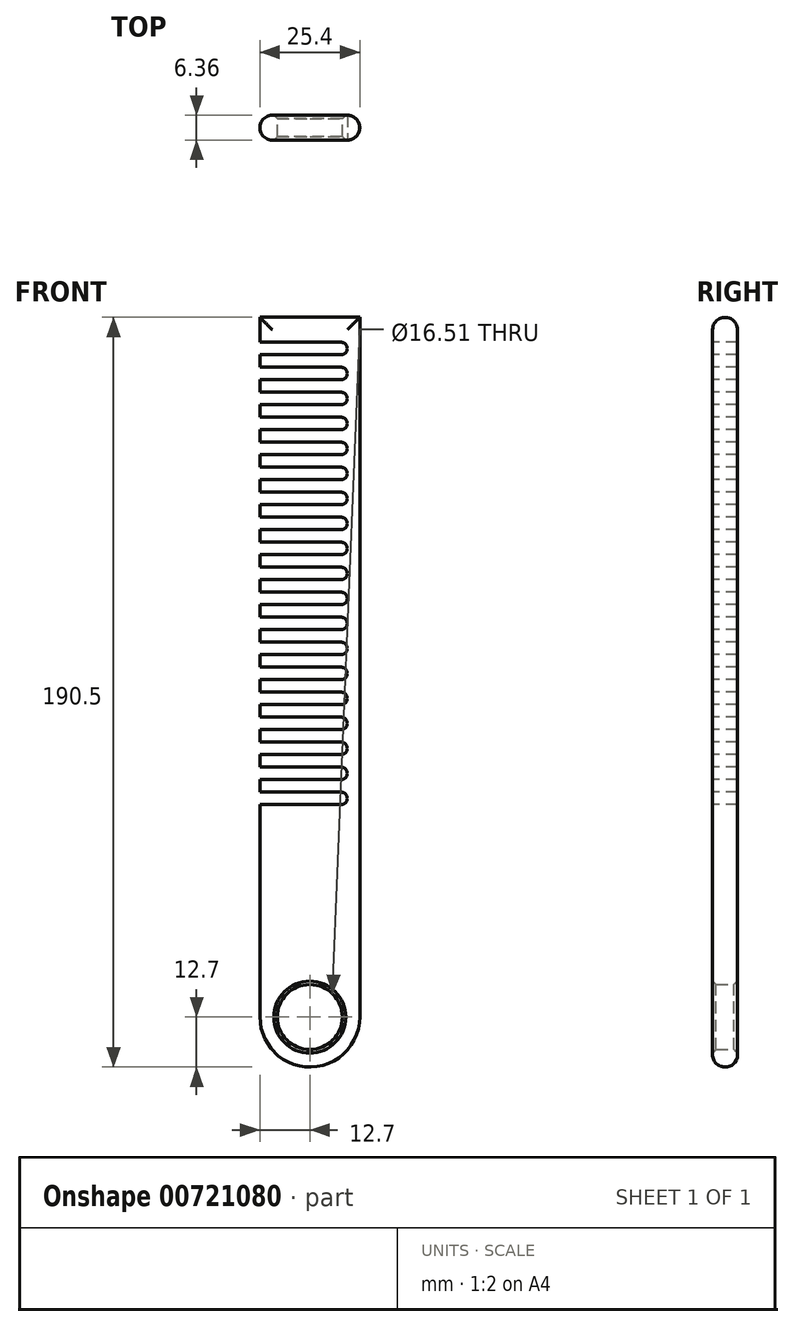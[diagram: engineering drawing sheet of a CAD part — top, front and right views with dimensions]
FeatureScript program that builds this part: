
annotation { "Feature Type Name" : "Feature", "Feature Type Description" : "" }
export const myFeature = defineFeature(function(context is Context, id is Id, definition is map)
    precondition{}
    {
        {
            var Q0;
            Q0=qCreatedBy(makeId("Front.planeOp"),FACE);
            var sketch = newSketch(context, id + "F0", { "sketchPlane" : qUnion([Q0])});
            skCircle(sketch, "E0", {"center": v(0, -63.5) * mm, "radius": 12.7 * mm});
            skCircle(sketch, "E1", {"center": v(0, -63.5) * mm, "radius": 8.26 * mm});
            skSolve(sketch);
        }
        {
            var Q0;
            Q0 = qSketchRegion(id + "F0", true);
            extrude(context, id + "F1", {"entities" : qUnion([Q0]), "endBound" : BoundingType.SYMMETRIC, "depth" : 6.35 * mm, "offsetDistance" : 25.4 * mm});
        }
        {
            var Q0;
            Q0=qCreatedBy(makeId("Front.planeOp"),FACE);
            var sketch = newSketch(context, id + "F2", { "sketchPlane" : qUnion([Q0])});
            skLineSegment(sketch, "E2.top", {"start": v(-12.7, 114.3) * mm, "end": v(12.7, 114.3) * mm});
            skLineSegment(sketch, "E2.left", {"start": v(-12.7, -63.5) * mm, "end": v(-12.7, 114.3) * mm});
            skLineSegment(sketch, "E2.right", {"start": v(12.7, -63.5) * mm, "end": v(12.7, 114.3) * mm});
            skPoint(sketch, "E2.middle", {"position": v(0, 0) * mm});
            skArc(sketch, "E3", {"start": v(12.7, -63.5) * mm, "mid": v(0, -50.8) * mm, "end": v(-12.7, -63.5) * mm});
            skPoint(sketch, "E2.bottom.end.orphan", {"position": v(12.7, -114.3) * mm});
            skPoint(sketch, "E2.bottom.start.orphan", {"position": v(-12.7, -114.3) * mm});
            skSolve(sketch);
        }
        {
            var Q0;
            Q0 = qSketchRegion(id + "F2", true);
            extrude(context, id + "F3", {"entities" : qUnion([Q0]), "operationType" : NewBodyOperationType.ADD, "endBound" : BoundingType.SYMMETRIC, "depth" : 6.35 * mm, "offsetDistance" : 25.4 * mm});
        }
        {
            var Q0;
            Q0=makeQuery(id+"F3.opExtrude","CAP_EDGE",EDGE,{"disambiguationData":[OSD([sQuery(id+"F2.wireOp",EDGE,"E2.right")])],"isStart":false});
            var Q1;
            Q1=makeQuery(id+"F3.opExtrude","CAP_EDGE",EDGE,{"disambiguationData":[OSD([sQuery(id+"F2.wireOp",EDGE,"E2.right")])],"isStart":true});
            var Q2;
            Q2=makeQuery(id+"F3.opExtrude","CAP_EDGE",EDGE,{"disambiguationData":[OSD([sQuery(id+"F2.wireOp",EDGE,"E2.top")])],"isStart":false});
            var Q3;
            Q3=makeQuery(id+"F3.opExtrude","CAP_EDGE",EDGE,{"disambiguationData":[OSD([sQuery(id+"F2.wireOp",EDGE,"E2.top")])],"isStart":true});
            fillet(context, id + "F4", {"entities" : qUnion([Q0, Q1, Q2, Q3]), "radius" : 3.17 * mm, "tangentPropagation" : true, "allowEdgeOverflow" : false});
        }
        {
            var Q0;
            Q0=makeQuery(id+"F1.opExtrude","CAP_EDGE",EDGE,{"disambiguationData":[OSD([sQuery(id+"F0.wireOp",EDGE,"E1")])],"isStart":false});
            var Q1;
            Q1=makeQuery(id+"F1.opExtrude","CAP_EDGE",EDGE,{"disambiguationData":[OSD([sQuery(id+"F0.wireOp",EDGE,"E1")])],"isStart":true});
            chamfer(context, id + "F5", {"entities" : qUnion([Q0, Q1]), "width" : 0.89 * mm, "tangentPropagation" : true});
        }
        {
            var Q0;
            Q0=makeQuery(id+"F3.boolean.opBoolean","MERGE",FACE,{"derivedFrom":[makeQuery(id+"F1.opExtrude","CAP_FACE",FACE,{"disambiguationData":[OSD([sQuery(id+"F0.wireOp",EDGE,"E0"),sQuery(id+"F0.wireOp",EDGE,"E1")])],"isStart":false}),makeQuery(id+"F3.opExtrude","CAP_FACE",FACE,{"disambiguationData":[OSD([sQuery(id+"F2.wireOp",EDGE,"E2.top"),sQuery(id+"F2.wireOp",EDGE,"E2.left"),sQuery(id+"F2.wireOp",EDGE,"E2.right"),sQuery(id+"F2.wireOp",EDGE,"E3")])],"isStart":false})]});
            var sketch = newSketch(context, id + "F6", { "sketchPlane" : qUnion([Q0])});
            skLineSegment(sketch, "E4", {"start": v(9.52, 111.12) * mm, "end": v(9.52, 107.95) * mm});
            skLineSegment(sketch, "E5", {"start": v(9.52, 111.12) * mm, "end": v(-9.53, 111.12) * mm});
            skLineSegment(sketch, "E6", {"start": v(9.52, 107.95) * mm, "end": v(-16.08, 107.95) * mm});
            skLineSegment(sketch, "E7", {"start": v(-16.08, 111.12) * mm, "end": v(-9.53, 111.12) * mm});
            skArc(sketch, "E8", {"start": v(-16.08, 111.12) * mm, "mid": v(-17.67, 109.54) * mm, "end": v(-16.08, 107.95) * mm});
            skPoint(sketch, "E9.center.orphan", {"position": v(0, -63.5) * mm});
            skLineSegment(sketch, "E10.0.1.0", {"start": v(9.52, 104.77) * mm, "end": v(9.52, 101.6) * mm});
            skLineSegment(sketch, "E10.0.1.1", {"start": v(9.52, 104.77) * mm, "end": v(-9.53, 104.77) * mm});
            skLineSegment(sketch, "E10.0.1.2", {"start": v(9.52, 101.6) * mm, "end": v(-16.08, 101.6) * mm});
            skArc(sketch, "E10.0.1.3", {"start": v(-16.08, 104.77) * mm, "mid": v(-17.67, 103.19) * mm, "end": v(-16.08, 101.6) * mm});
            skLineSegment(sketch, "E10.0.1.4", {"start": v(-16.08, 104.77) * mm, "end": v(-9.53, 104.77) * mm});
            skLineSegment(sketch, "E10.0.2.0", {"start": v(9.52, 98.42) * mm, "end": v(9.52, 95.25) * mm});
            skLineSegment(sketch, "E10.0.2.1", {"start": v(9.52, 98.42) * mm, "end": v(-9.53, 98.42) * mm});
            skLineSegment(sketch, "E10.0.2.2", {"start": v(9.52, 95.25) * mm, "end": v(-16.08, 95.25) * mm});
            skArc(sketch, "E10.0.2.3", {"start": v(-16.08, 98.42) * mm, "mid": v(-17.67, 96.84) * mm, "end": v(-16.08, 95.25) * mm});
            skLineSegment(sketch, "E10.0.2.4", {"start": v(-16.08, 98.42) * mm, "end": v(-9.53, 98.42) * mm});
            skLineSegment(sketch, "E10.direction1", {"start": v(9.52, 107.95) * mm, "end": v(-15.88, 107.95) * mm, "construction": true});
            skLineSegment(sketch, "E10.direction2", {"start": v(9.52, 107.95) * mm, "end": v(9.52, 101.6) * mm, "construction": true});
            skLineSegment(sketch, "E11.0.0.3", {"start": v(9.52, 92.07) * mm, "end": v(9.52, 88.9) * mm});
            skLineSegment(sketch, "E11.3.0.3", {"start": v(9.52, 92.07) * mm, "end": v(-9.53, 92.07) * mm});
            skLineSegment(sketch, "E11.6.0.3", {"start": v(9.52, 88.9) * mm, "end": v(-16.08, 88.9) * mm});
            skArc(sketch, "E11.9.0.3", {"start": v(-16.08, 92.07) * mm, "mid": v(-17.67, 90.49) * mm, "end": v(-16.08, 88.9) * mm});
            skLineSegment(sketch, "E11.13.0.3", {"start": v(-16.08, 92.07) * mm, "end": v(-9.53, 92.07) * mm});
            skLineSegment(sketch, "E11.0.0.4", {"start": v(9.52, 85.72) * mm, "end": v(9.52, 82.55) * mm});
            skLineSegment(sketch, "E11.3.0.4", {"start": v(9.52, 85.72) * mm, "end": v(-9.53, 85.72) * mm});
            skLineSegment(sketch, "E11.6.0.4", {"start": v(9.52, 82.55) * mm, "end": v(-16.08, 82.55) * mm});
            skArc(sketch, "E11.9.0.4", {"start": v(-16.08, 85.72) * mm, "mid": v(-17.67, 84.14) * mm, "end": v(-16.08, 82.55) * mm});
            skLineSegment(sketch, "E11.13.0.4", {"start": v(-16.08, 85.72) * mm, "end": v(-9.53, 85.72) * mm});
            skLineSegment(sketch, "E12.0.0.5", {"start": v(9.52, 79.37) * mm, "end": v(9.52, 76.2) * mm});
            skLineSegment(sketch, "E12.3.0.5", {"start": v(9.52, 79.37) * mm, "end": v(-9.53, 79.37) * mm});
            skLineSegment(sketch, "E12.6.0.5", {"start": v(9.52, 76.2) * mm, "end": v(-16.08, 76.2) * mm});
            skArc(sketch, "E12.9.0.5", {"start": v(-16.08, 79.37) * mm, "mid": v(-17.67, 77.79) * mm, "end": v(-16.08, 76.2) * mm});
            skLineSegment(sketch, "E12.13.0.5", {"start": v(-16.08, 79.37) * mm, "end": v(-9.53, 79.37) * mm});
            skLineSegment(sketch, "E12.0.0.6", {"start": v(9.52, 73.02) * mm, "end": v(9.52, 69.85) * mm});
            skLineSegment(sketch, "E12.3.0.6", {"start": v(9.52, 73.02) * mm, "end": v(-9.53, 73.02) * mm});
            skLineSegment(sketch, "E12.6.0.6", {"start": v(9.52, 69.85) * mm, "end": v(-16.08, 69.85) * mm});
            skArc(sketch, "E12.9.0.6", {"start": v(-16.08, 73.02) * mm, "mid": v(-17.67, 71.44) * mm, "end": v(-16.08, 69.85) * mm});
            skLineSegment(sketch, "E12.13.0.6", {"start": v(-16.08, 73.02) * mm, "end": v(-9.53, 73.02) * mm});
            skLineSegment(sketch, "E12.0.0.7", {"start": v(9.52, 66.67) * mm, "end": v(9.52, 63.5) * mm});
            skLineSegment(sketch, "E12.3.0.7", {"start": v(9.52, 66.67) * mm, "end": v(-9.53, 66.67) * mm});
            skLineSegment(sketch, "E12.6.0.7", {"start": v(9.52, 63.5) * mm, "end": v(-16.08, 63.5) * mm});
            skArc(sketch, "E12.9.0.7", {"start": v(-16.08, 66.67) * mm, "mid": v(-17.67, 65.09) * mm, "end": v(-16.08, 63.5) * mm});
            skLineSegment(sketch, "E12.13.0.7", {"start": v(-16.08, 66.67) * mm, "end": v(-9.53, 66.67) * mm});
            skLineSegment(sketch, "E12.0.0.8", {"start": v(9.52, 60.32) * mm, "end": v(9.52, 57.15) * mm});
            skLineSegment(sketch, "E12.3.0.8", {"start": v(9.52, 60.32) * mm, "end": v(-9.53, 60.32) * mm});
            skLineSegment(sketch, "E12.6.0.8", {"start": v(9.52, 57.15) * mm, "end": v(-16.08, 57.15) * mm});
            skArc(sketch, "E12.9.0.8", {"start": v(-16.08, 60.32) * mm, "mid": v(-17.67, 58.74) * mm, "end": v(-16.08, 57.15) * mm});
            skLineSegment(sketch, "E12.13.0.8", {"start": v(-16.08, 60.32) * mm, "end": v(-9.53, 60.32) * mm});
            skLineSegment(sketch, "E12.0.0.9", {"start": v(9.52, 53.97) * mm, "end": v(9.52, 50.8) * mm});
            skLineSegment(sketch, "E12.3.0.9", {"start": v(9.52, 53.97) * mm, "end": v(-9.53, 53.97) * mm});
            skLineSegment(sketch, "E12.6.0.9", {"start": v(9.52, 50.8) * mm, "end": v(-16.08, 50.8) * mm});
            skArc(sketch, "E12.9.0.9", {"start": v(-16.08, 53.97) * mm, "mid": v(-17.67, 52.39) * mm, "end": v(-16.08, 50.8) * mm});
            skLineSegment(sketch, "E12.13.0.9", {"start": v(-16.08, 53.97) * mm, "end": v(-9.53, 53.97) * mm});
            skLineSegment(sketch, "E13.0.0.10", {"start": v(9.52, 47.62) * mm, "end": v(9.52, 44.45) * mm});
            skLineSegment(sketch, "E13.3.0.10", {"start": v(9.52, 47.62) * mm, "end": v(-9.53, 47.62) * mm});
            skLineSegment(sketch, "E13.6.0.10", {"start": v(9.52, 44.45) * mm, "end": v(-16.08, 44.45) * mm});
            skArc(sketch, "E13.9.0.10", {"start": v(-16.08, 47.62) * mm, "mid": v(-17.67, 46.04) * mm, "end": v(-16.08, 44.45) * mm});
            skLineSegment(sketch, "E13.13.0.10", {"start": v(-16.08, 47.62) * mm, "end": v(-9.53, 47.62) * mm});
            skLineSegment(sketch, "E13.0.0.11", {"start": v(9.52, 41.27) * mm, "end": v(9.52, 38.1) * mm});
            skLineSegment(sketch, "E13.3.0.11", {"start": v(9.52, 41.27) * mm, "end": v(-9.53, 41.27) * mm});
            skLineSegment(sketch, "E13.6.0.11", {"start": v(9.52, 38.1) * mm, "end": v(-16.08, 38.1) * mm});
            skArc(sketch, "E13.9.0.11", {"start": v(-16.08, 41.27) * mm, "mid": v(-17.67, 39.69) * mm, "end": v(-16.08, 38.1) * mm});
            skLineSegment(sketch, "E13.13.0.11", {"start": v(-16.08, 41.27) * mm, "end": v(-9.53, 41.27) * mm});
            skLineSegment(sketch, "E13.0.0.12", {"start": v(9.52, 34.92) * mm, "end": v(9.52, 31.75) * mm});
            skLineSegment(sketch, "E13.3.0.12", {"start": v(9.52, 34.92) * mm, "end": v(-9.53, 34.92) * mm});
            skLineSegment(sketch, "E13.6.0.12", {"start": v(9.52, 31.75) * mm, "end": v(-16.08, 31.75) * mm});
            skArc(sketch, "E13.9.0.12", {"start": v(-16.08, 34.92) * mm, "mid": v(-17.67, 33.34) * mm, "end": v(-16.08, 31.75) * mm});
            skLineSegment(sketch, "E13.13.0.12", {"start": v(-16.08, 34.92) * mm, "end": v(-9.53, 34.92) * mm});
            skLineSegment(sketch, "E13.0.0.13", {"start": v(9.52, 28.57) * mm, "end": v(9.52, 25.4) * mm});
            skLineSegment(sketch, "E13.3.0.13", {"start": v(9.52, 28.57) * mm, "end": v(-9.53, 28.57) * mm});
            skLineSegment(sketch, "E13.6.0.13", {"start": v(9.52, 25.4) * mm, "end": v(-16.08, 25.4) * mm});
            skArc(sketch, "E13.9.0.13", {"start": v(-16.08, 28.57) * mm, "mid": v(-17.67, 26.99) * mm, "end": v(-16.08, 25.4) * mm});
            skLineSegment(sketch, "E13.13.0.13", {"start": v(-16.08, 28.57) * mm, "end": v(-9.53, 28.57) * mm});
            skLineSegment(sketch, "E13.0.0.14", {"start": v(9.52, 22.22) * mm, "end": v(9.52, 19.05) * mm});
            skLineSegment(sketch, "E13.3.0.14", {"start": v(9.52, 22.22) * mm, "end": v(-9.53, 22.22) * mm});
            skLineSegment(sketch, "E13.6.0.14", {"start": v(9.52, 19.05) * mm, "end": v(-16.08, 19.05) * mm});
            skArc(sketch, "E13.9.0.14", {"start": v(-16.08, 22.22) * mm, "mid": v(-17.67, 20.64) * mm, "end": v(-16.08, 19.05) * mm});
            skLineSegment(sketch, "E13.13.0.14", {"start": v(-16.08, 22.22) * mm, "end": v(-9.53, 22.22) * mm});
            skLineSegment(sketch, "E14.0.0.15", {"start": v(9.52, 15.87) * mm, "end": v(9.52, 12.7) * mm});
            skLineSegment(sketch, "E14.3.0.15", {"start": v(9.52, 15.87) * mm, "end": v(-9.53, 15.87) * mm});
            skLineSegment(sketch, "E14.6.0.15", {"start": v(9.52, 12.7) * mm, "end": v(-16.08, 12.7) * mm});
            skArc(sketch, "E14.9.0.15", {"start": v(-16.08, 15.87) * mm, "mid": v(-17.67, 14.29) * mm, "end": v(-16.08, 12.7) * mm});
            skLineSegment(sketch, "E14.13.0.15", {"start": v(-16.08, 15.87) * mm, "end": v(-9.53, 15.87) * mm});
            skLineSegment(sketch, "E14.0.0.16", {"start": v(9.52, 9.52) * mm, "end": v(9.52, 6.35) * mm});
            skLineSegment(sketch, "E14.3.0.16", {"start": v(9.52, 9.52) * mm, "end": v(-9.53, 9.52) * mm});
            skLineSegment(sketch, "E14.6.0.16", {"start": v(9.52, 6.35) * mm, "end": v(-16.08, 6.35) * mm});
            skArc(sketch, "E14.9.0.16", {"start": v(-16.08, 9.52) * mm, "mid": v(-17.67, 7.94) * mm, "end": v(-16.08, 6.35) * mm});
            skLineSegment(sketch, "E14.13.0.16", {"start": v(-16.08, 9.52) * mm, "end": v(-9.53, 9.52) * mm});
            skLineSegment(sketch, "E14.0.0.17", {"start": v(9.52, 3.17) * mm, "end": v(9.52, 0) * mm});
            skLineSegment(sketch, "E14.3.0.17", {"start": v(9.52, 3.17) * mm, "end": v(-9.53, 3.17) * mm});
            skLineSegment(sketch, "E14.6.0.17", {"start": v(9.52, 0) * mm, "end": v(-16.08, 0) * mm});
            skArc(sketch, "E14.9.0.17", {"start": v(-16.08, 3.17) * mm, "mid": v(-17.67, 1.59) * mm, "end": v(-16.08, 0) * mm});
            skLineSegment(sketch, "E14.13.0.17", {"start": v(-16.08, 3.17) * mm, "end": v(-9.53, 3.17) * mm});
            skLineSegment(sketch, "E14.0.0.18", {"start": v(9.52, -3.18) * mm, "end": v(9.52, -6.35) * mm});
            skLineSegment(sketch, "E14.3.0.18", {"start": v(9.52, -3.18) * mm, "end": v(-9.53, -3.18) * mm});
            skLineSegment(sketch, "E14.6.0.18", {"start": v(9.52, -6.35) * mm, "end": v(-16.08, -6.35) * mm});
            skArc(sketch, "E14.9.0.18", {"start": v(-16.08, -3.18) * mm, "mid": v(-17.67, -4.76) * mm, "end": v(-16.08, -6.35) * mm});
            skLineSegment(sketch, "E14.13.0.18", {"start": v(-16.08, -3.18) * mm, "end": v(-9.53, -3.18) * mm});
            skLineSegment(sketch, "E14.0.0.19", {"start": v(9.52, -9.53) * mm, "end": v(9.52, -12.7) * mm});
            skLineSegment(sketch, "E14.3.0.19", {"start": v(9.52, -9.53) * mm, "end": v(-9.53, -9.53) * mm});
            skLineSegment(sketch, "E14.6.0.19", {"start": v(9.52, -12.7) * mm, "end": v(-16.08, -12.7) * mm});
            skArc(sketch, "E14.9.0.19", {"start": v(-16.08, -9.53) * mm, "mid": v(-17.67, -11.11) * mm, "end": v(-16.08, -12.7) * mm});
            skLineSegment(sketch, "E14.13.0.19", {"start": v(-16.08, -9.53) * mm, "end": v(-9.53, -9.53) * mm});
            skLineSegment(sketch, "E15", {"start": v(9.52, 111.12) * mm, "end": v(9.52, -12.7) * mm});
            skLineSegment(sketch, "E16", {"start": v(-12.8, 111.12) * mm, "end": v(-12.8, -12.7) * mm});
            skSolve(sketch);
        }
        {
            var Q0;
            {var subQ6=sQuery(id+"F6.wireOp",EDGE,"E10.0.1.1");Q0=makeQuery(id+"F6.imprint","IMPRINT",FACE,{"disambiguationData":[TD([[makeQuery(id+"F6.imprint","IMPRINT",EDGE,{"derivedFrom":subQ6}),-1.0]])]});}
            var Q1;
            {var subQ5=sQuery(id+"F6.wireOp",EDGE,"E10.0.2.1");Q1=makeQuery(id+"F6.imprint","IMPRINT",FACE,{"disambiguationData":[TD([[makeQuery(id+"F6.imprint","IMPRINT",EDGE,{"derivedFrom":subQ5}),-1.0]])]});}
            var Q2;
            {var subQ5=sQuery(id+"F6.wireOp",EDGE,"E11.3.0.3");Q2=makeQuery(id+"F6.imprint","IMPRINT",FACE,{"disambiguationData":[TD([[makeQuery(id+"F6.imprint","IMPRINT",EDGE,{"derivedFrom":subQ5}),-1.0]])]});}
            var Q3;
            {var subQ5=sQuery(id+"F6.wireOp",EDGE,"E11.3.0.4");Q3=makeQuery(id+"F6.imprint","IMPRINT",FACE,{"disambiguationData":[TD([[makeQuery(id+"F6.imprint","IMPRINT",EDGE,{"derivedFrom":subQ5}),-1.0]])]});}
            var Q4;
            {var subQ5=sQuery(id+"F6.wireOp",EDGE,"E12.3.0.5");Q4=makeQuery(id+"F6.imprint","IMPRINT",FACE,{"disambiguationData":[TD([[makeQuery(id+"F6.imprint","IMPRINT",EDGE,{"derivedFrom":subQ5}),-1.0]])]});}
            var Q5;
            {var subQ5=sQuery(id+"F6.wireOp",EDGE,"E12.3.0.6");Q5=makeQuery(id+"F6.imprint","IMPRINT",FACE,{"disambiguationData":[TD([[makeQuery(id+"F6.imprint","IMPRINT",EDGE,{"derivedFrom":subQ5}),-1.0]])]});}
            var Q6;
            {var subQ5=sQuery(id+"F6.wireOp",EDGE,"E12.3.0.7");Q6=makeQuery(id+"F6.imprint","IMPRINT",FACE,{"disambiguationData":[TD([[makeQuery(id+"F6.imprint","IMPRINT",EDGE,{"derivedFrom":subQ5}),-1.0]])]});}
            var Q7;
            {var subQ5=sQuery(id+"F6.wireOp",EDGE,"E12.3.0.8");Q7=makeQuery(id+"F6.imprint","IMPRINT",FACE,{"disambiguationData":[TD([[makeQuery(id+"F6.imprint","IMPRINT",EDGE,{"derivedFrom":subQ5}),-1.0]])]});}
            var Q8;
            {var subQ5=sQuery(id+"F6.wireOp",EDGE,"E12.3.0.9");Q8=makeQuery(id+"F6.imprint","IMPRINT",FACE,{"disambiguationData":[TD([[makeQuery(id+"F6.imprint","IMPRINT",EDGE,{"derivedFrom":subQ5}),-1.0]])]});}
            var Q9;
            {var subQ5=sQuery(id+"F6.wireOp",EDGE,"E13.3.0.10");Q9=makeQuery(id+"F6.imprint","IMPRINT",FACE,{"disambiguationData":[TD([[makeQuery(id+"F6.imprint","IMPRINT",EDGE,{"derivedFrom":subQ5}),-1.0]])]});}
            var Q10;
            {var subQ5=sQuery(id+"F6.wireOp",EDGE,"E13.3.0.11");Q10=makeQuery(id+"F6.imprint","IMPRINT",FACE,{"disambiguationData":[TD([[makeQuery(id+"F6.imprint","IMPRINT",EDGE,{"derivedFrom":subQ5}),-1.0]])]});}
            var Q11;
            {var subQ5=sQuery(id+"F6.wireOp",EDGE,"E13.3.0.12");Q11=makeQuery(id+"F6.imprint","IMPRINT",FACE,{"disambiguationData":[TD([[makeQuery(id+"F6.imprint","IMPRINT",EDGE,{"derivedFrom":subQ5}),-1.0]])]});}
            var Q12;
            {var subQ5=sQuery(id+"F6.wireOp",EDGE,"E13.3.0.13");Q12=makeQuery(id+"F6.imprint","IMPRINT",FACE,{"disambiguationData":[TD([[makeQuery(id+"F6.imprint","IMPRINT",EDGE,{"derivedFrom":subQ5}),-1.0]])]});}
            var Q13;
            {var subQ5=sQuery(id+"F6.wireOp",EDGE,"E13.3.0.14");Q13=makeQuery(id+"F6.imprint","IMPRINT",FACE,{"disambiguationData":[TD([[makeQuery(id+"F6.imprint","IMPRINT",EDGE,{"derivedFrom":subQ5}),-1.0]])]});}
            var Q14;
            {var subQ5=sQuery(id+"F6.wireOp",EDGE,"E14.3.0.15");Q14=makeQuery(id+"F6.imprint","IMPRINT",FACE,{"disambiguationData":[TD([[makeQuery(id+"F6.imprint","IMPRINT",EDGE,{"derivedFrom":subQ5}),-1.0]])]});}
            var Q15;
            {var subQ5=sQuery(id+"F6.wireOp",EDGE,"E14.3.0.16");Q15=makeQuery(id+"F6.imprint","IMPRINT",FACE,{"disambiguationData":[TD([[makeQuery(id+"F6.imprint","IMPRINT",EDGE,{"derivedFrom":subQ5}),-1.0]])]});}
            var Q16;
            {var subQ5=sQuery(id+"F6.wireOp",EDGE,"E14.3.0.17");Q16=makeQuery(id+"F6.imprint","IMPRINT",FACE,{"disambiguationData":[TD([[makeQuery(id+"F6.imprint","IMPRINT",EDGE,{"derivedFrom":subQ5}),-1.0]])]});}
            var Q17;
            {var subQ5=sQuery(id+"F6.wireOp",EDGE,"E14.3.0.18");Q17=makeQuery(id+"F6.imprint","IMPRINT",FACE,{"disambiguationData":[TD([[makeQuery(id+"F6.imprint","IMPRINT",EDGE,{"derivedFrom":subQ5}),-1.0]])]});}
            var Q18;
            {var subQ5=sQuery(id+"F6.wireOp",EDGE,"E14.3.0.19");Q18=makeQuery(id+"F6.imprint","IMPRINT",FACE,{"disambiguationData":[TD([[makeQuery(id+"F6.imprint","IMPRINT",EDGE,{"derivedFrom":subQ5}),-1.0]])]});}
            var Q19;
            {var subQ0=sQuery(id+"F6.wireOp",EDGE,"E16");var subQ1=sQuery(id+"F6.wireOp",EDGE,"E6");var subQ2=makeQuery(id+"F6.imprint","INTERSECT",VERTEX,{"derivedFrom":[subQ1,subQ0]});Q19=makeQuery(id+"F6.imprint","IMPRINT",FACE,{"disambiguationData":[TD([[makeQuery(id+"F6.imprint","IMPRINT",EDGE,{"disambiguationData":[TD([[subQ2,-1.0]])],"derivedFrom":subQ0}),1.0]])]});}
            var Q20;
            {var subQ0=sQuery(id+"F6.wireOp",EDGE,"E16");var subQ1=sQuery(id+"F6.wireOp",EDGE,"E10.0.1.2");var subQ2=makeQuery(id+"F6.imprint","INTERSECT",VERTEX,{"derivedFrom":[subQ1,subQ0]});Q20=makeQuery(id+"F6.imprint","IMPRINT",FACE,{"disambiguationData":[TD([[makeQuery(id+"F6.imprint","IMPRINT",EDGE,{"disambiguationData":[TD([[subQ2,-1.0]])],"derivedFrom":subQ0}),1.0]])]});}
            var Q21;
            {var subQ0=sQuery(id+"F6.wireOp",EDGE,"E16");var subQ1=sQuery(id+"F6.wireOp",EDGE,"E10.0.2.2");var subQ2=makeQuery(id+"F6.imprint","INTERSECT",VERTEX,{"derivedFrom":[subQ1,subQ0]});Q21=makeQuery(id+"F6.imprint","IMPRINT",FACE,{"disambiguationData":[TD([[makeQuery(id+"F6.imprint","IMPRINT",EDGE,{"disambiguationData":[TD([[subQ2,-1.0]])],"derivedFrom":subQ0}),1.0]])]});}
            var Q22;
            {var subQ0=sQuery(id+"F6.wireOp",EDGE,"E16");var subQ1=sQuery(id+"F6.wireOp",EDGE,"E11.6.0.3");var subQ2=makeQuery(id+"F6.imprint","INTERSECT",VERTEX,{"derivedFrom":[subQ1,subQ0]});Q22=makeQuery(id+"F6.imprint","IMPRINT",FACE,{"disambiguationData":[TD([[makeQuery(id+"F6.imprint","IMPRINT",EDGE,{"disambiguationData":[TD([[subQ2,-1.0]])],"derivedFrom":subQ0}),1.0]])]});}
            var Q23;
            {var subQ0=sQuery(id+"F6.wireOp",EDGE,"E16");var subQ1=sQuery(id+"F6.wireOp",EDGE,"E11.6.0.4");var subQ2=makeQuery(id+"F6.imprint","INTERSECT",VERTEX,{"derivedFrom":[subQ1,subQ0]});Q23=makeQuery(id+"F6.imprint","IMPRINT",FACE,{"disambiguationData":[TD([[makeQuery(id+"F6.imprint","IMPRINT",EDGE,{"disambiguationData":[TD([[subQ2,-1.0]])],"derivedFrom":subQ0}),1.0]])]});}
            var Q24;
            {var subQ0=sQuery(id+"F6.wireOp",EDGE,"E16");var subQ1=sQuery(id+"F6.wireOp",EDGE,"E12.6.0.5");var subQ2=makeQuery(id+"F6.imprint","INTERSECT",VERTEX,{"derivedFrom":[subQ1,subQ0]});Q24=makeQuery(id+"F6.imprint","IMPRINT",FACE,{"disambiguationData":[TD([[makeQuery(id+"F6.imprint","IMPRINT",EDGE,{"disambiguationData":[TD([[subQ2,-1.0]])],"derivedFrom":subQ0}),1.0]])]});}
            var Q25;
            {var subQ0=sQuery(id+"F6.wireOp",EDGE,"E16");var subQ1=sQuery(id+"F6.wireOp",EDGE,"E14.6.0.18");var subQ2=makeQuery(id+"F6.imprint","INTERSECT",VERTEX,{"derivedFrom":[subQ1,subQ0]});Q25=makeQuery(id+"F6.imprint","IMPRINT",FACE,{"disambiguationData":[TD([[makeQuery(id+"F6.imprint","IMPRINT",EDGE,{"disambiguationData":[TD([[subQ2,-1.0]])],"derivedFrom":subQ0}),1.0]])]});}
            var Q26;
            {var subQ0=sQuery(id+"F6.wireOp",EDGE,"E16");var subQ1=sQuery(id+"F6.wireOp",EDGE,"E14.6.0.17");var subQ2=makeQuery(id+"F6.imprint","INTERSECT",VERTEX,{"derivedFrom":[subQ1,subQ0]});Q26=makeQuery(id+"F6.imprint","IMPRINT",FACE,{"disambiguationData":[TD([[makeQuery(id+"F6.imprint","IMPRINT",EDGE,{"disambiguationData":[TD([[subQ2,-1.0]])],"derivedFrom":subQ0}),1.0]])]});}
            var Q27;
            {var subQ0=sQuery(id+"F6.wireOp",EDGE,"E16");var subQ1=sQuery(id+"F6.wireOp",EDGE,"E14.6.0.16");var subQ2=makeQuery(id+"F6.imprint","INTERSECT",VERTEX,{"derivedFrom":[subQ1,subQ0]});Q27=makeQuery(id+"F6.imprint","IMPRINT",FACE,{"disambiguationData":[TD([[makeQuery(id+"F6.imprint","IMPRINT",EDGE,{"disambiguationData":[TD([[subQ2,-1.0]])],"derivedFrom":subQ0}),1.0]])]});}
            var Q28;
            {var subQ0=sQuery(id+"F6.wireOp",EDGE,"E16");var subQ1=sQuery(id+"F6.wireOp",EDGE,"E14.6.0.15");var subQ2=makeQuery(id+"F6.imprint","INTERSECT",VERTEX,{"derivedFrom":[subQ1,subQ0]});Q28=makeQuery(id+"F6.imprint","IMPRINT",FACE,{"disambiguationData":[TD([[makeQuery(id+"F6.imprint","IMPRINT",EDGE,{"disambiguationData":[TD([[subQ2,-1.0]])],"derivedFrom":subQ0}),1.0]])]});}
            var Q29;
            {var subQ0=sQuery(id+"F6.wireOp",EDGE,"E16");var subQ1=sQuery(id+"F6.wireOp",EDGE,"E13.6.0.14");var subQ2=makeQuery(id+"F6.imprint","INTERSECT",VERTEX,{"derivedFrom":[subQ1,subQ0]});Q29=makeQuery(id+"F6.imprint","IMPRINT",FACE,{"disambiguationData":[TD([[makeQuery(id+"F6.imprint","IMPRINT",EDGE,{"disambiguationData":[TD([[subQ2,-1.0]])],"derivedFrom":subQ0}),1.0]])]});}
            var Q30;
            {var subQ0=sQuery(id+"F6.wireOp",EDGE,"E16");var subQ1=sQuery(id+"F6.wireOp",EDGE,"E13.6.0.13");var subQ2=makeQuery(id+"F6.imprint","INTERSECT",VERTEX,{"derivedFrom":[subQ1,subQ0]});Q30=makeQuery(id+"F6.imprint","IMPRINT",FACE,{"disambiguationData":[TD([[makeQuery(id+"F6.imprint","IMPRINT",EDGE,{"disambiguationData":[TD([[subQ2,-1.0]])],"derivedFrom":subQ0}),1.0]])]});}
            var Q31;
            {var subQ0=sQuery(id+"F6.wireOp",EDGE,"E16");var subQ1=sQuery(id+"F6.wireOp",EDGE,"E13.6.0.12");var subQ2=makeQuery(id+"F6.imprint","INTERSECT",VERTEX,{"derivedFrom":[subQ1,subQ0]});Q31=makeQuery(id+"F6.imprint","IMPRINT",FACE,{"disambiguationData":[TD([[makeQuery(id+"F6.imprint","IMPRINT",EDGE,{"disambiguationData":[TD([[subQ2,-1.0]])],"derivedFrom":subQ0}),1.0]])]});}
            var Q32;
            {var subQ0=sQuery(id+"F6.wireOp",EDGE,"E16");var subQ1=sQuery(id+"F6.wireOp",EDGE,"E13.6.0.11");var subQ2=makeQuery(id+"F6.imprint","INTERSECT",VERTEX,{"derivedFrom":[subQ1,subQ0]});Q32=makeQuery(id+"F6.imprint","IMPRINT",FACE,{"disambiguationData":[TD([[makeQuery(id+"F6.imprint","IMPRINT",EDGE,{"disambiguationData":[TD([[subQ2,-1.0]])],"derivedFrom":subQ0}),1.0]])]});}
            var Q33;
            {var subQ0=sQuery(id+"F6.wireOp",EDGE,"E16");var subQ1=sQuery(id+"F6.wireOp",EDGE,"E13.6.0.10");var subQ2=makeQuery(id+"F6.imprint","INTERSECT",VERTEX,{"derivedFrom":[subQ1,subQ0]});Q33=makeQuery(id+"F6.imprint","IMPRINT",FACE,{"disambiguationData":[TD([[makeQuery(id+"F6.imprint","IMPRINT",EDGE,{"disambiguationData":[TD([[subQ2,-1.0]])],"derivedFrom":subQ0}),1.0]])]});}
            var Q34;
            {var subQ0=sQuery(id+"F6.wireOp",EDGE,"E16");var subQ1=sQuery(id+"F6.wireOp",EDGE,"E12.6.0.9");var subQ2=makeQuery(id+"F6.imprint","INTERSECT",VERTEX,{"derivedFrom":[subQ1,subQ0]});Q34=makeQuery(id+"F6.imprint","IMPRINT",FACE,{"disambiguationData":[TD([[makeQuery(id+"F6.imprint","IMPRINT",EDGE,{"disambiguationData":[TD([[subQ2,-1.0]])],"derivedFrom":subQ0}),1.0]])]});}
            var Q35;
            {var subQ0=sQuery(id+"F6.wireOp",EDGE,"E16");var subQ1=sQuery(id+"F6.wireOp",EDGE,"E12.6.0.8");var subQ2=makeQuery(id+"F6.imprint","INTERSECT",VERTEX,{"derivedFrom":[subQ1,subQ0]});Q35=makeQuery(id+"F6.imprint","IMPRINT",FACE,{"disambiguationData":[TD([[makeQuery(id+"F6.imprint","IMPRINT",EDGE,{"disambiguationData":[TD([[subQ2,-1.0]])],"derivedFrom":subQ0}),1.0]])]});}
            var Q36;
            {var subQ0=sQuery(id+"F6.wireOp",EDGE,"E16");var subQ1=sQuery(id+"F6.wireOp",EDGE,"E12.6.0.7");var subQ2=makeQuery(id+"F6.imprint","INTERSECT",VERTEX,{"derivedFrom":[subQ1,subQ0]});Q36=makeQuery(id+"F6.imprint","IMPRINT",FACE,{"disambiguationData":[TD([[makeQuery(id+"F6.imprint","IMPRINT",EDGE,{"disambiguationData":[TD([[subQ2,-1.0]])],"derivedFrom":subQ0}),1.0]])]});}
            var Q37;
            {var subQ0=sQuery(id+"F6.wireOp",EDGE,"E16");var subQ1=sQuery(id+"F6.wireOp",EDGE,"E12.6.0.6");var subQ2=makeQuery(id+"F6.imprint","INTERSECT",VERTEX,{"derivedFrom":[subQ1,subQ0]});Q37=makeQuery(id+"F6.imprint","IMPRINT",FACE,{"disambiguationData":[TD([[makeQuery(id+"F6.imprint","IMPRINT",EDGE,{"disambiguationData":[TD([[subQ2,-1.0]])],"derivedFrom":subQ0}),1.0]])]});}
            extrude(context, id + "F7", {"entities" : qUnion([Q0, Q1, Q2, Q3, Q4, Q5, Q6, Q7, Q8, Q9, Q10, Q11, Q12, Q13, Q14, Q15, Q16, Q17, Q18, Q19, Q20, Q21, Q22, Q23, Q24, Q25, Q26, Q27, Q28, Q29, Q30, Q31, Q32, Q33, Q34, Q35, Q36, Q37]), "operationType" : NewBodyOperationType.REMOVE, "oppositeDirection" : true, "depth" : 25.4 * mm, "offsetDistance" : 25.4 * mm});
        }
        {
            var Q0;
            Q0=makeQuery(id+"F7.boolean.opBoolean","COPY",EDGE,{"derivedFrom":makeQuery(id+"F7.opExtrude","SWEPT_EDGE",EDGE,{"disambiguationData":[OSD([sQuery(id+"F6.wireOp",EDGE,"E6"),sQuery(id+"F6.wireOp",EDGE,"E15")])]})});
            var Q1;
            Q1=makeQuery(id+"F7.boolean.opBoolean","COPY",EDGE,{"derivedFrom":makeQuery(id+"F7.opExtrude","SWEPT_EDGE",EDGE,{"disambiguationData":[OSD([sQuery(id+"F6.wireOp",EDGE,"E10.0.1.1"),sQuery(id+"F6.wireOp",EDGE,"E15")])]})});
            var Q2;
            Q2=makeQuery(id+"F7.boolean.opBoolean","COPY",EDGE,{"derivedFrom":makeQuery(id+"F7.opExtrude","SWEPT_EDGE",EDGE,{"disambiguationData":[OSD([sQuery(id+"F6.wireOp",EDGE,"E10.0.1.2"),sQuery(id+"F6.wireOp",EDGE,"E15")])]})});
            var Q3;
            Q3=makeQuery(id+"F7.boolean.opBoolean","COPY",EDGE,{"derivedFrom":makeQuery(id+"F7.opExtrude","SWEPT_EDGE",EDGE,{"disambiguationData":[OSD([sQuery(id+"F6.wireOp",EDGE,"E10.0.2.1"),sQuery(id+"F6.wireOp",EDGE,"E15")])]})});
            var Q4;
            Q4=makeQuery(id+"F7.boolean.opBoolean","COPY",EDGE,{"derivedFrom":makeQuery(id+"F7.opExtrude","SWEPT_EDGE",EDGE,{"disambiguationData":[OSD([sQuery(id+"F6.wireOp",EDGE,"E11.3.0.3"),sQuery(id+"F6.wireOp",EDGE,"E15")])]})});
            var Q5;
            Q5=makeQuery(id+"F7.boolean.opBoolean","COPY",EDGE,{"derivedFrom":makeQuery(id+"F7.opExtrude","SWEPT_EDGE",EDGE,{"disambiguationData":[OSD([sQuery(id+"F6.wireOp",EDGE,"E11.3.0.4"),sQuery(id+"F6.wireOp",EDGE,"E15")])]})});
            var Q6;
            Q6=makeQuery(id+"F7.boolean.opBoolean","COPY",EDGE,{"derivedFrom":makeQuery(id+"F7.opExtrude","SWEPT_EDGE",EDGE,{"disambiguationData":[OSD([sQuery(id+"F6.wireOp",EDGE,"E12.3.0.5"),sQuery(id+"F6.wireOp",EDGE,"E15")])]})});
            var Q7;
            Q7=makeQuery(id+"F7.boolean.opBoolean","COPY",EDGE,{"derivedFrom":makeQuery(id+"F7.opExtrude","SWEPT_EDGE",EDGE,{"disambiguationData":[OSD([sQuery(id+"F6.wireOp",EDGE,"E12.3.0.6"),sQuery(id+"F6.wireOp",EDGE,"E15")])]})});
            var Q8;
            Q8=makeQuery(id+"F7.boolean.opBoolean","COPY",EDGE,{"derivedFrom":makeQuery(id+"F7.opExtrude","SWEPT_EDGE",EDGE,{"disambiguationData":[OSD([sQuery(id+"F6.wireOp",EDGE,"E12.3.0.7"),sQuery(id+"F6.wireOp",EDGE,"E15")])]})});
            var Q9;
            Q9=makeQuery(id+"F7.boolean.opBoolean","COPY",EDGE,{"derivedFrom":makeQuery(id+"F7.opExtrude","SWEPT_EDGE",EDGE,{"disambiguationData":[OSD([sQuery(id+"F6.wireOp",EDGE,"E12.3.0.8"),sQuery(id+"F6.wireOp",EDGE,"E15")])]})});
            var Q10;
            Q10=makeQuery(id+"F7.boolean.opBoolean","COPY",EDGE,{"derivedFrom":makeQuery(id+"F7.opExtrude","SWEPT_EDGE",EDGE,{"disambiguationData":[OSD([sQuery(id+"F6.wireOp",EDGE,"E12.3.0.9"),sQuery(id+"F6.wireOp",EDGE,"E15")])]})});
            var Q11;
            Q11=makeQuery(id+"F7.boolean.opBoolean","COPY",EDGE,{"derivedFrom":makeQuery(id+"F7.opExtrude","SWEPT_EDGE",EDGE,{"disambiguationData":[OSD([sQuery(id+"F6.wireOp",EDGE,"E13.3.0.10"),sQuery(id+"F6.wireOp",EDGE,"E15")])]})});
            var Q12;
            Q12=makeQuery(id+"F7.boolean.opBoolean","COPY",EDGE,{"derivedFrom":makeQuery(id+"F7.opExtrude","SWEPT_EDGE",EDGE,{"disambiguationData":[OSD([sQuery(id+"F6.wireOp",EDGE,"E13.3.0.11"),sQuery(id+"F6.wireOp",EDGE,"E15")])]})});
            var Q13;
            Q13=makeQuery(id+"F7.boolean.opBoolean","COPY",EDGE,{"derivedFrom":makeQuery(id+"F7.opExtrude","SWEPT_EDGE",EDGE,{"disambiguationData":[OSD([sQuery(id+"F6.wireOp",EDGE,"E13.3.0.12"),sQuery(id+"F6.wireOp",EDGE,"E15")])]})});
            var Q14;
            Q14=makeQuery(id+"F7.boolean.opBoolean","COPY",EDGE,{"derivedFrom":makeQuery(id+"F7.opExtrude","SWEPT_EDGE",EDGE,{"disambiguationData":[OSD([sQuery(id+"F6.wireOp",EDGE,"E13.3.0.13"),sQuery(id+"F6.wireOp",EDGE,"E15")])]})});
            var Q15;
            Q15=makeQuery(id+"F7.boolean.opBoolean","COPY",EDGE,{"derivedFrom":makeQuery(id+"F7.opExtrude","SWEPT_EDGE",EDGE,{"disambiguationData":[OSD([sQuery(id+"F6.wireOp",EDGE,"E13.3.0.14"),sQuery(id+"F6.wireOp",EDGE,"E15")])]})});
            var Q16;
            Q16=makeQuery(id+"F7.boolean.opBoolean","COPY",EDGE,{"derivedFrom":makeQuery(id+"F7.opExtrude","SWEPT_EDGE",EDGE,{"disambiguationData":[OSD([sQuery(id+"F6.wireOp",EDGE,"E14.3.0.15"),sQuery(id+"F6.wireOp",EDGE,"E15")])]})});
            var Q17;
            Q17=makeQuery(id+"F7.boolean.opBoolean","COPY",EDGE,{"derivedFrom":makeQuery(id+"F7.opExtrude","SWEPT_EDGE",EDGE,{"disambiguationData":[OSD([sQuery(id+"F6.wireOp",EDGE,"E14.3.0.16"),sQuery(id+"F6.wireOp",EDGE,"E15")])]})});
            var Q18;
            Q18=makeQuery(id+"F7.boolean.opBoolean","COPY",EDGE,{"derivedFrom":makeQuery(id+"F7.opExtrude","SWEPT_EDGE",EDGE,{"disambiguationData":[OSD([sQuery(id+"F6.wireOp",EDGE,"E14.3.0.17"),sQuery(id+"F6.wireOp",EDGE,"E15")])]})});
            var Q19;
            Q19=makeQuery(id+"F7.boolean.opBoolean","COPY",EDGE,{"derivedFrom":makeQuery(id+"F7.opExtrude","SWEPT_EDGE",EDGE,{"disambiguationData":[OSD([sQuery(id+"F6.wireOp",EDGE,"E14.3.0.18"),sQuery(id+"F6.wireOp",EDGE,"E15")])]})});
            var Q20;
            Q20=makeQuery(id+"F7.boolean.opBoolean","COPY",EDGE,{"derivedFrom":makeQuery(id+"F7.opExtrude","SWEPT_EDGE",EDGE,{"disambiguationData":[OSD([sQuery(id+"F6.wireOp",EDGE,"E14.3.0.19"),sQuery(id+"F6.wireOp",EDGE,"E15")])]})});
            var Q21;
            Q21=makeQuery(id+"F7.boolean.opBoolean","COPY",EDGE,{"derivedFrom":makeQuery(id+"F7.opExtrude","SWEPT_EDGE",EDGE,{"disambiguationData":[OSD([sQuery(id+"F6.wireOp",EDGE,"E14.6.0.18"),sQuery(id+"F6.wireOp",EDGE,"E15")])]})});
            var Q22;
            Q22=makeQuery(id+"F7.boolean.opBoolean","COPY",EDGE,{"derivedFrom":makeQuery(id+"F7.opExtrude","SWEPT_EDGE",EDGE,{"disambiguationData":[OSD([sQuery(id+"F6.wireOp",EDGE,"E14.6.0.17"),sQuery(id+"F6.wireOp",EDGE,"E15")])]})});
            var Q23;
            Q23=makeQuery(id+"F7.boolean.opBoolean","COPY",EDGE,{"derivedFrom":makeQuery(id+"F7.opExtrude","SWEPT_EDGE",EDGE,{"disambiguationData":[OSD([sQuery(id+"F6.wireOp",EDGE,"E14.6.0.16"),sQuery(id+"F6.wireOp",EDGE,"E15")])]})});
            var Q24;
            Q24=makeQuery(id+"F7.boolean.opBoolean","COPY",EDGE,{"derivedFrom":makeQuery(id+"F7.opExtrude","SWEPT_EDGE",EDGE,{"disambiguationData":[OSD([sQuery(id+"F6.wireOp",EDGE,"E14.6.0.15"),sQuery(id+"F6.wireOp",EDGE,"E15")])]})});
            var Q25;
            Q25=makeQuery(id+"F7.boolean.opBoolean","COPY",EDGE,{"derivedFrom":makeQuery(id+"F7.opExtrude","SWEPT_EDGE",EDGE,{"disambiguationData":[OSD([sQuery(id+"F6.wireOp",EDGE,"E13.6.0.14"),sQuery(id+"F6.wireOp",EDGE,"E15")])]})});
            var Q26;
            Q26=makeQuery(id+"F7.boolean.opBoolean","COPY",EDGE,{"derivedFrom":makeQuery(id+"F7.opExtrude","SWEPT_EDGE",EDGE,{"disambiguationData":[OSD([sQuery(id+"F6.wireOp",EDGE,"E13.6.0.13"),sQuery(id+"F6.wireOp",EDGE,"E15")])]})});
            var Q27;
            Q27=makeQuery(id+"F7.boolean.opBoolean","COPY",EDGE,{"derivedFrom":makeQuery(id+"F7.opExtrude","SWEPT_EDGE",EDGE,{"disambiguationData":[OSD([sQuery(id+"F6.wireOp",EDGE,"E13.6.0.12"),sQuery(id+"F6.wireOp",EDGE,"E15")])]})});
            var Q28;
            Q28=makeQuery(id+"F7.boolean.opBoolean","COPY",EDGE,{"derivedFrom":makeQuery(id+"F7.opExtrude","SWEPT_EDGE",EDGE,{"disambiguationData":[OSD([sQuery(id+"F6.wireOp",EDGE,"E13.6.0.11"),sQuery(id+"F6.wireOp",EDGE,"E15")])]})});
            var Q29;
            Q29=makeQuery(id+"F7.boolean.opBoolean","COPY",EDGE,{"derivedFrom":makeQuery(id+"F7.opExtrude","SWEPT_EDGE",EDGE,{"disambiguationData":[OSD([sQuery(id+"F6.wireOp",EDGE,"E13.6.0.10"),sQuery(id+"F6.wireOp",EDGE,"E15")])]})});
            var Q30;
            Q30=makeQuery(id+"F7.boolean.opBoolean","COPY",EDGE,{"derivedFrom":makeQuery(id+"F7.opExtrude","SWEPT_EDGE",EDGE,{"disambiguationData":[OSD([sQuery(id+"F6.wireOp",EDGE,"E12.6.0.9"),sQuery(id+"F6.wireOp",EDGE,"E15")])]})});
            var Q31;
            Q31=makeQuery(id+"F7.boolean.opBoolean","COPY",EDGE,{"derivedFrom":makeQuery(id+"F7.opExtrude","SWEPT_EDGE",EDGE,{"disambiguationData":[OSD([sQuery(id+"F6.wireOp",EDGE,"E12.6.0.8"),sQuery(id+"F6.wireOp",EDGE,"E15")])]})});
            var Q32;
            Q32=makeQuery(id+"F7.boolean.opBoolean","COPY",EDGE,{"derivedFrom":makeQuery(id+"F7.opExtrude","SWEPT_EDGE",EDGE,{"disambiguationData":[OSD([sQuery(id+"F6.wireOp",EDGE,"E12.6.0.7"),sQuery(id+"F6.wireOp",EDGE,"E15")])]})});
            var Q33;
            Q33=makeQuery(id+"F7.boolean.opBoolean","COPY",EDGE,{"derivedFrom":makeQuery(id+"F7.opExtrude","SWEPT_EDGE",EDGE,{"disambiguationData":[OSD([sQuery(id+"F6.wireOp",EDGE,"E12.6.0.6"),sQuery(id+"F6.wireOp",EDGE,"E15")])]})});
            var Q34;
            Q34=makeQuery(id+"F7.boolean.opBoolean","COPY",EDGE,{"derivedFrom":makeQuery(id+"F7.opExtrude","SWEPT_EDGE",EDGE,{"disambiguationData":[OSD([sQuery(id+"F6.wireOp",EDGE,"E12.6.0.5"),sQuery(id+"F6.wireOp",EDGE,"E15")])]})});
            var Q35;
            Q35=makeQuery(id+"F7.boolean.opBoolean","COPY",EDGE,{"derivedFrom":makeQuery(id+"F7.opExtrude","SWEPT_EDGE",EDGE,{"disambiguationData":[OSD([sQuery(id+"F6.wireOp",EDGE,"E11.6.0.4"),sQuery(id+"F6.wireOp",EDGE,"E15")])]})});
            var Q36;
            Q36=makeQuery(id+"F7.boolean.opBoolean","COPY",EDGE,{"derivedFrom":makeQuery(id+"F7.opExtrude","SWEPT_EDGE",EDGE,{"disambiguationData":[OSD([sQuery(id+"F6.wireOp",EDGE,"E11.6.0.3"),sQuery(id+"F6.wireOp",EDGE,"E15")])]})});
            var Q37;
            Q37=makeQuery(id+"F7.boolean.opBoolean","COPY",EDGE,{"derivedFrom":makeQuery(id+"F7.opExtrude","SWEPT_EDGE",EDGE,{"disambiguationData":[OSD([sQuery(id+"F6.wireOp",EDGE,"E10.0.2.2"),sQuery(id+"F6.wireOp",EDGE,"E15")])]})});
            fillet(context, id + "F8", {"entities" : qUnion([Q0, Q1, Q2, Q3, Q4, Q5, Q6, Q7, Q8, Q9, Q10, Q11, Q12, Q13, Q14, Q15, Q16, Q17, Q18, Q19, Q20, Q21, Q22, Q23, Q24, Q25, Q26, Q27, Q28, Q29, Q30, Q31, Q32, Q33, Q34, Q35, Q36, Q37]), "radius" : 1.59 * mm, "tangentPropagation" : true, "allowEdgeOverflow" : false});
        }
    });
